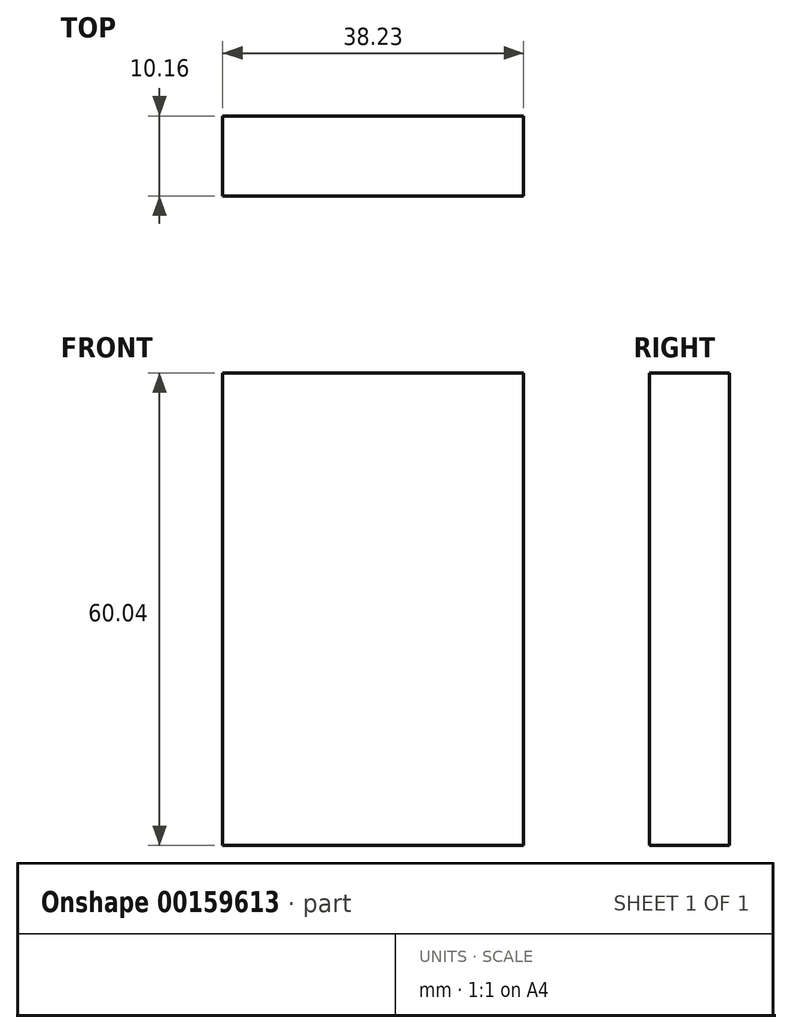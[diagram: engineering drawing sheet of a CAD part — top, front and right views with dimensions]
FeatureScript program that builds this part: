
annotation { "Feature Type Name" : "Feature", "Feature Type Description" : "" }
export const myFeature = defineFeature(function(context is Context, id is Id, definition is map)
    precondition{}
    {
        {
            var Q0;
            Q0=qCreatedBy(makeId("Front.planeOp"),FACE);
            var sketch = newSketch(context, id + "F0", { "sketchPlane" : qUnion([Q0])});
            skLineSegment(sketch, "E0.bottom", {"start": v(-40.31, 32.96) * mm, "end": v(-2.08, 32.96) * mm});
            skLineSegment(sketch, "E0.top", {"start": v(-40.31, -27.08) * mm, "end": v(-2.08, -27.08) * mm});
            skLineSegment(sketch, "E0.left", {"start": v(-40.31, 32.96) * mm, "end": v(-40.31, -27.08) * mm});
            skLineSegment(sketch, "E0.right", {"start": v(-2.08, 32.96) * mm, "end": v(-2.08, -27.08) * mm});
            skSolve(sketch);
        }
        {
            var Q0;
            Q0 = qSketchRegion(id + "F0", true);
            extrude(context, id + "F1", {"entities" : qUnion([Q0]), "endBound" : BoundingType.SYMMETRIC, "depth" : 10.16 * mm});
        }
    });
